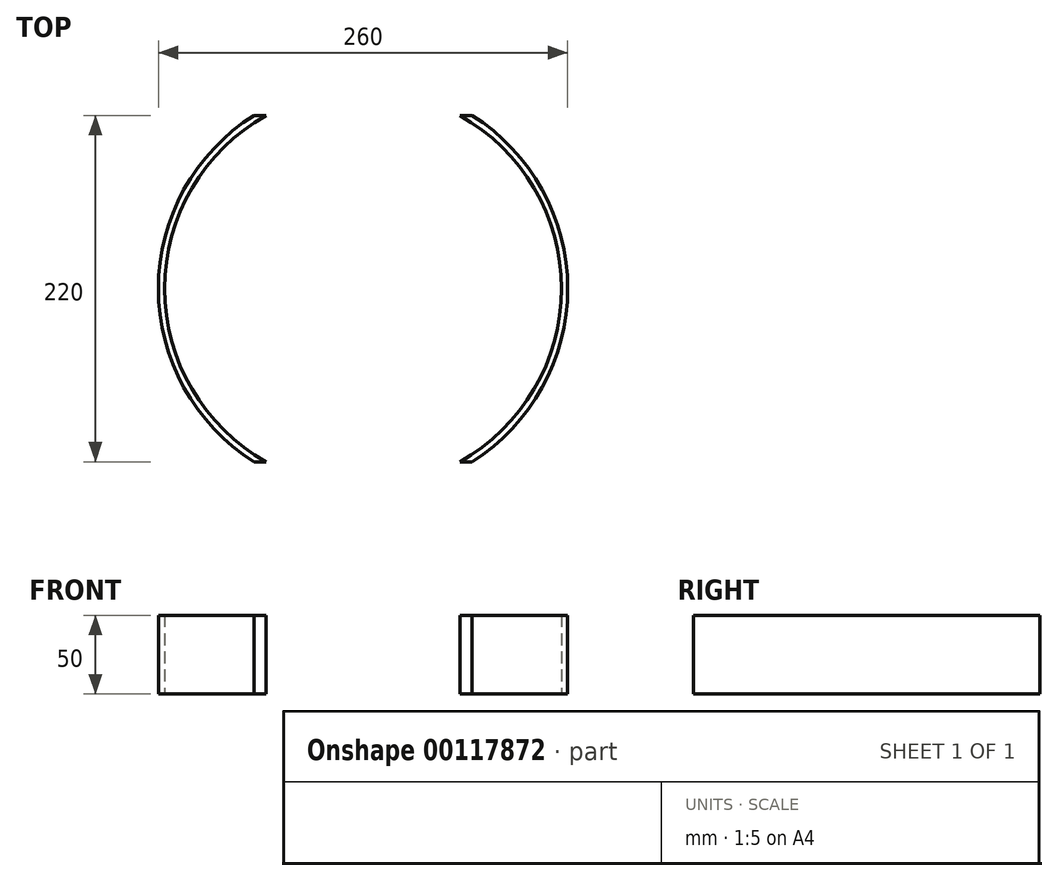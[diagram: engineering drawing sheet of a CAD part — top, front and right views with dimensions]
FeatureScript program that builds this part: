
annotation { "Feature Type Name" : "Feature", "Feature Type Description" : "" }
export const myFeature = defineFeature(function(context is Context, id is Id, definition is map)
    precondition{}
    {
        {
            var Q0;
            Q0=qCreatedBy(makeId("Top.planeOp"),FACE);
            var sketch = newSketch(context, id + "F0", { "sketchPlane" : qUnion([Q0])});
            skArc(sketch, "E0", {"start": v(-69.28, 110) * mm, "mid": v(-130, 0) * mm, "end": v(-69.28, -110) * mm});
            skArc(sketch, "E1", {"start": v(69.28, -110) * mm, "mid": v(130, 0) * mm, "end": v(69.28, 110) * mm});
            skArc(sketch, "E2", {"start": v(-61.45, 110) * mm, "mid": v(-126, 0) * mm, "end": v(-61.45, -110) * mm});
            skArc(sketch, "E3", {"start": v(61.45, -110) * mm, "mid": v(126, 0) * mm, "end": v(61.45, 110) * mm});
            skLineSegment(sketch, "E4", {"start": v(-69.28, 110) * mm, "end": v(-61.45, 110) * mm});
            skLineSegment(sketch, "E5", {"start": v(61.45, 110) * mm, "end": v(69.28, 110) * mm});
            skLineSegment(sketch, "E6", {"start": v(-69.28, -110) * mm, "end": v(-61.45, -110) * mm});
            skLineSegment(sketch, "E7", {"start": v(61.45, -110) * mm, "end": v(69.28, -110) * mm});
            skSolve(sketch);
        }
        {
            var Q0;
            Q0=makeQuery(id+"F0.imprint","IMPRINT",FACE,{"disambiguationData":[TD([[makeQuery(id+"F0.imprint","IMPRINT",EDGE,{"derivedFrom":sQuery(id+"F0.wireOp",EDGE,"E0")}),1.0]])]});
            var Q1;
            Q1=makeQuery(id+"F0.imprint","IMPRINT",FACE,{"disambiguationData":[TD([[makeQuery(id+"F0.imprint","IMPRINT",EDGE,{"derivedFrom":sQuery(id+"F0.wireOp",EDGE,"E1")}),1.0]])]});
            extrude(context, id + "F1", {"entities" : qUnion([Q0, Q1]), "depth" : 50 * mm});
        }
    });
